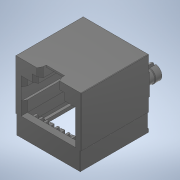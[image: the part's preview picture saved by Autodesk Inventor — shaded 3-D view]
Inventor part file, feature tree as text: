
AUTODESK INVENTOR PART (.ipt)
format: ipt  version: 2020.1 (Build 241239000, 239)  size: 667,136 bytes
history: native  units: mm
features: chamfer x31, extrude x18, sketch x18, projected_geometry x2, mirror x1, fillet x1, plane x1
ambient origin geometry x8: Origin, YZ Plane, XZ Plane, XY Plane, X Axis, Y Axis, Z Axis, Center Point
bodies: Solid1 (feature_tree)
feature tree (72):
  extrude  "Extrusion1"  Depth=15.5mm
  extrude  "Extrusion2"  Depth=4.35mm
  extrude  "Extrusion3"  Depth=6.64mm
  chamfer  "Chamfer1"  Distance=12.7mm
  chamfer  "Chamfer2"  Distance=1.65mm
  chamfer  "Chamfer3"  Distance=0.5mm Angle=45.0deg
  chamfer  "Chamfer4"  Distance=0.5mm Angle=45.0deg
  chamfer  "Chamfer5"  Distance=0.5mm Angle=45.0deg
  chamfer  "Chamfer6"  Distance=0.5mm Angle=45.0deg
  chamfer  "Chamfer7"  Distance=0.5mm Angle=45.0deg
  chamfer  "Chamfer8"  Distance=0.5mm Angle=45.0deg
  chamfer  "Chamfer9"  Distance=0.5mm Angle=45.0deg
  chamfer  "Chamfer10"  Distance=0.5mm Angle=45.0deg
  chamfer  "Chamfer11"  Distance=0.5mm Angle=45.0deg
  chamfer  "Chamfer12"  Distance=0.5mm Angle=45.0deg
  chamfer  "Chamfer13"  Distance=0.5mm Angle=45.0deg
  extrude  "Extrusion4"  Depth=0.5mm TaperAngle=45.0deg
  extrude  "Extrusion5"  Depth=1.0mm TaperAngle=0.0deg
  chamfer  "Chamfer14"  Distance=3.0mm
  extrude  "Extrusion6"  Depth=8.95mm
  extrude  "Extrusion7"  Depth=2.3mm
  extrude  "Extrusion8"  Depth=12.85mm
  extrude  "Extrusion9"  Depth=2.9mm
  extrude  "Extrusion10"  Depth=2.9mm
  chamfer  "Chamfer15"  Distance=7.675mm
  chamfer  "Chamfer16"  Distance=1.1mm
  chamfer  "Chamfer17"  Distance=5.0mm
  chamfer  "Chamfer18"  Distance=10.9mm
  chamfer  "Chamfer19"  Distance=2.9mm
  chamfer  "Chamfer20"  Distance=1.2mm
  chamfer  "Chamfer21"  Distance=11.2mm
  chamfer  "Chamfer22"  Distance=0.45mm
  chamfer  "Chamfer23"  Distance=4.35mm
  chamfer  "Chamfer24"  Distance=3.08mm
  chamfer  "Chamfer25"  Distance=10.0mm
  chamfer  "Chamfer26"  Distance=10.0mm
  chamfer  "Chamfer27"  Distance=0.9mm Angle=45.0deg
  extrude  "Extrusion11"  Depth=2.9mm TaperAngle=45.0deg
  extrude  "Extrusion12"  Depth=2.9mm TaperAngle=45.0deg
  extrude  "Extrusion13"  Depth=2.9mm TaperAngle=45.0deg
  extrude  "Extrusion14"  Depth=2.9mm TaperAngle=45.0deg
  extrude  "Extrusion15"  Depth=2.9mm TaperAngle=45.0deg
  chamfer  "Chamfer28"  Distance=0.9mm Angle=45.0deg
  chamfer  "Chamfer29"  Distance=0.9mm Angle=45.0deg
  chamfer  "Chamfer30"  Distance=0.9mm Angle=45.0deg
  extrude  "Extrusion16"  Depth=2.9mm TaperAngle=45.0deg
  mirror  "Mirror1"
  extrude  "Extrusion17"  Depth=2.9mm TaperAngle=45.0deg
  extrude  "Extrusion18"  Depth=2.9mm TaperAngle=45.0deg
  fillet  "Fillet1"  Radius=0.9mm
  chamfer  "Chamfer31"  Distance=10.0mm
  sketch  "Sketch1"  dims[d5=16.25mm d6=15.5mm]
  sketch  "Sketch2"  dims[d7=15.08mm d8=4.35mm]
  sketch  "Sketch3"  dims[d9=16.0mm d10=0.0mm d12=6.64mm]
  sketch  "Sketch4"  dims[d13=12.85mm]
  sketch  "Sketch5"  dims[d14=11.85mm]
  sketch  "Sketch6"  dims[d15=7.25mm]
  sketch  "Sketch8"  dims[d16=2.85mm]
  sketch  "Sketch9"  dims[d17=2.6mm]
  projected_geometry  "Projected Loop1"
  sketch  "Sketch10"  dims[d18=8.95mm]
  sketch  "Sketch11"  dims[d19=5.0mm d20=12.7mm d21=0.0mm]
  sketch  "Sketch12"  dims[d22=4.36mm d23=1.65mm d24=0.0mm d25=0.5mm d26=1.0mm d27=45.0deg d28=0.5mm d29=1.0mm d30=45.0deg d31=0.5mm d32=1.0mm d33=45.0deg d34=0.5mm d35=1.0mm d36=45.0deg d37=0.5mm d38=1.0mm d39=45.0deg d40=0.5mm d41=1.0mm d42=45.0deg d43=0.5mm d44=1.0mm d45=45.0deg d46=0.5mm d47=1.0mm d48=45.0deg d49=0.5mm d50=1.0mm d51=45.0deg d52=0.5mm d53=1.0mm d54=45.0deg d55=0.5mm d56=1.0mm d57=45.0deg]
  sketch  "Sketch13"  dims[d58=0.5mm d59=1.0mm d60=45.0deg d61=0.5mm d62=1.0mm d63=45.0deg]
  sketch  "Sketch14"  dims[d64=1.87mm d65=1.0mm d66=0.0mm]
  sketch  "Sketch15"  dims[d67=1.55mm d68=3.0mm d69=0.0mm]
  sketch  "Sketch16"  dims[d70=0.32mm d71=0.95mm d72=45.0deg d74=8.95mm d75=7.98mm]
  sketch  "Sketch17"  dims[d76=12.85mm d77=2.3mm d78=6.475mm]
  plane  "Work Plane1"
  sketch  "Sketch19"  dims[d79=1.2mm d80=0.0mm d81=12.85mm]
  projected_geometry  "Projected Loop4"
  sketch  "Sketch20"  dims[d82=14.12mm d83=1.4mm d84=0.8mm d85=7.675mm d86=1.1mm d87=5.0mm d88=10.9mm d89=0.0mm d90=2.9mm d91=0.0mm d92=1.2mm d93=11.2mm d94=0.0mm d95=0.45mm d96=4.35mm d97=3.08mm d98=80.0mm d100=1.27mm d101=10.0mm d103=10.0mm d105=10.0mm d106=0.0mm d107=0.9mm d108=2.1mm d109=45.0deg d110=0.9mm d111=2.1mm d112=45.0deg d113=0.9mm d114=2.1mm d115=45.0deg d116=0.9mm d117=2.1mm d118=45.0deg d119=0.9mm d120=2.1mm d121=45.0deg d122=0.9mm d123=2.1mm d124=45.0deg d125=0.9mm d126=2.1mm d127=45.0deg d128=0.9mm d129=2.1mm d130=45.0deg d131=0.9mm d132=2.1mm d133=45.0deg d134=0.9mm d135=2.1mm d136=45.0deg d137=0.9mm d138=2.1mm d139=45.0deg d140=0.9mm d141=2.1mm d142=45.0deg d143=0.9mm d144=2.1mm d145=45.0deg d146=10.0mm d147=0.0mm d148=10.0mm d149=0.0mm d150=1.9mm d151=4.95mm d154=2.475mm d155=0.2mm d156=0.0mm d157=1.575mm d158=2.035mm d159=0.7mm d160=1.65mm d161=0.0mm d162=3.45mm d163=1.85mm d164=0.0mm d165=0.15mm d166=2.1mm d167=45.0deg d168=0.6mm d169=0.3mm d170=45.0deg d171=0.6mm d172=0.3mm d173=45.0deg d174=0.9mm d175=1.15mm d176=1.45mm d177=0.2mm d178=0.0mm d179=1.5mm d180=8.44mm d181=2.0mm d182=80.0mm d184=1.27mm d185=10.0mm d187=10.0mm d189=0.8mm d190=0.0mm d191=0.45mm d192=0.45mm d193=40.0mm d195=2.54mm d196=10.0mm d198=10.0mm d200=0.125mm d201=20.0mm d203=1.72mm d204=10.0mm d206=10.0mm d208=2.9mm d209=0.0mm d210=0.1mm d211=0.05mm d212=0.3mm d213=45.0deg]
